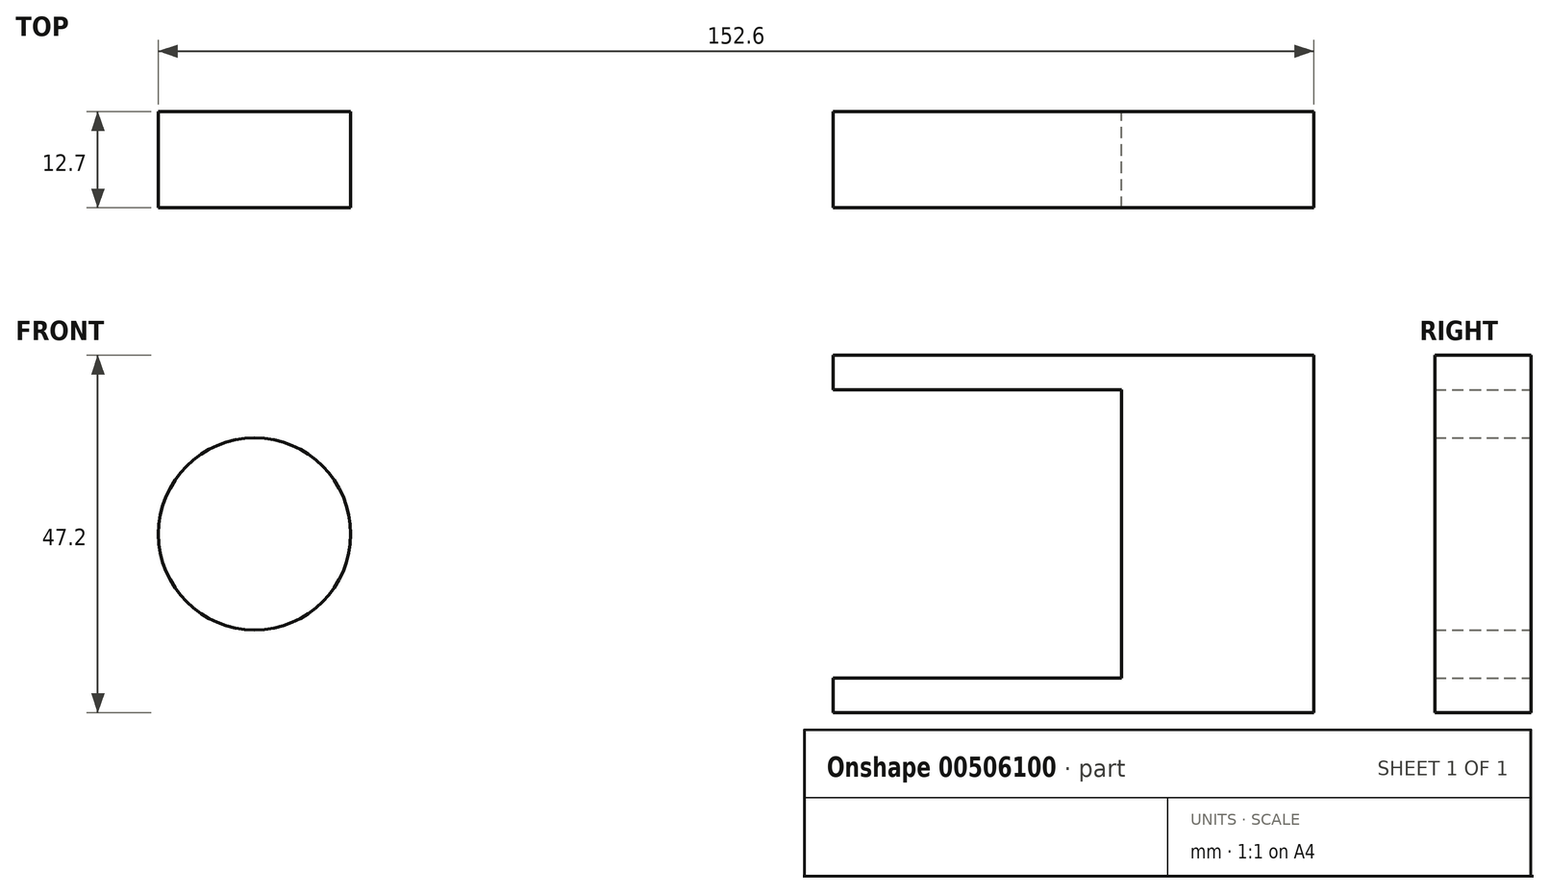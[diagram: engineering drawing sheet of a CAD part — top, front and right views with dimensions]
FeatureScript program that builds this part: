
annotation { "Feature Type Name" : "Feature", "Feature Type Description" : "" }
export const myFeature = defineFeature(function(context is Context, id is Id, definition is map)
    precondition{}
    {
        {
            var Q0;
            Q0=qCreatedBy(makeId("Front.planeOp"),FACE);
            var sketch = newSketch(context, id + "F0", { "sketchPlane" : qUnion([Q0])});
            skLineSegment(sketch, "E0", {"start": v(38.1, 0) * mm, "end": v(38.1, 19.05) * mm});
            skLineSegment(sketch, "E1", {"start": v(38.1, 19.05) * mm, "end": v(0, 19.05) * mm});
            skLineSegment(sketch, "E2", {"start": v(0, 19.05) * mm, "end": v(0, 23.6) * mm});
            skLineSegment(sketch, "E3", {"start": v(0, 23.6) * mm, "end": v(63.5, 23.6) * mm});
            skLineSegment(sketch, "E4", {"start": v(63.5, 23.6) * mm, "end": v(63.5, 0) * mm});
            skLineSegment(sketch, "E5", {"start": v(63.5, 0) * mm, "end": v(38.1, 0) * mm, "construction": true});
            skLineSegment(sketch, "E6.MirrorCS", {"start": v(63.5, -23.6) * mm, "end": v(63.5, 0) * mm});
            skLineSegment(sketch, "E7.MirrorCS", {"start": v(0, -23.6) * mm, "end": v(63.5, -23.6) * mm});
            skLineSegment(sketch, "E8.MirrorCS", {"start": v(0, -19.05) * mm, "end": v(0, -23.6) * mm});
            skLineSegment(sketch, "E9.MirrorCS", {"start": v(38.1, -19.05) * mm, "end": v(0, -19.05) * mm});
            skLineSegment(sketch, "E10.MirrorCS", {"start": v(38.1, 0) * mm, "end": v(38.1, -19.05) * mm});
            skSolve(sketch);
        }
        {
            var Q0;
            Q0=qCreatedBy(makeId("Front.planeOp"),FACE);
            var sketch = newSketch(context, id + "F1", { "sketchPlane" : qUnion([Q0])});
            skCircle(sketch, "E11", {"center": v(-76.4, 0) * mm, "radius": 12.7 * mm});
            skSolve(sketch);
        }
        {
            var Q0;
            Q0 = qSketchRegion(id + "F0", true);
            var Q1;
            Q1=makeQuery(id+"F1.imprint","IMPRINT",FACE,{"disambiguationData":[TD([[makeQuery(id+"F1.imprint","IMPRINT",EDGE,{"derivedFrom":sQuery(id+"F1.wireOp",EDGE,"E11")}),1.0]])]});
            extrude(context, id + "F2", {"entities" : qUnion([Q0, Q1]), "depth" : 12.7 * mm, "symmetric" : true});
        }
    });
